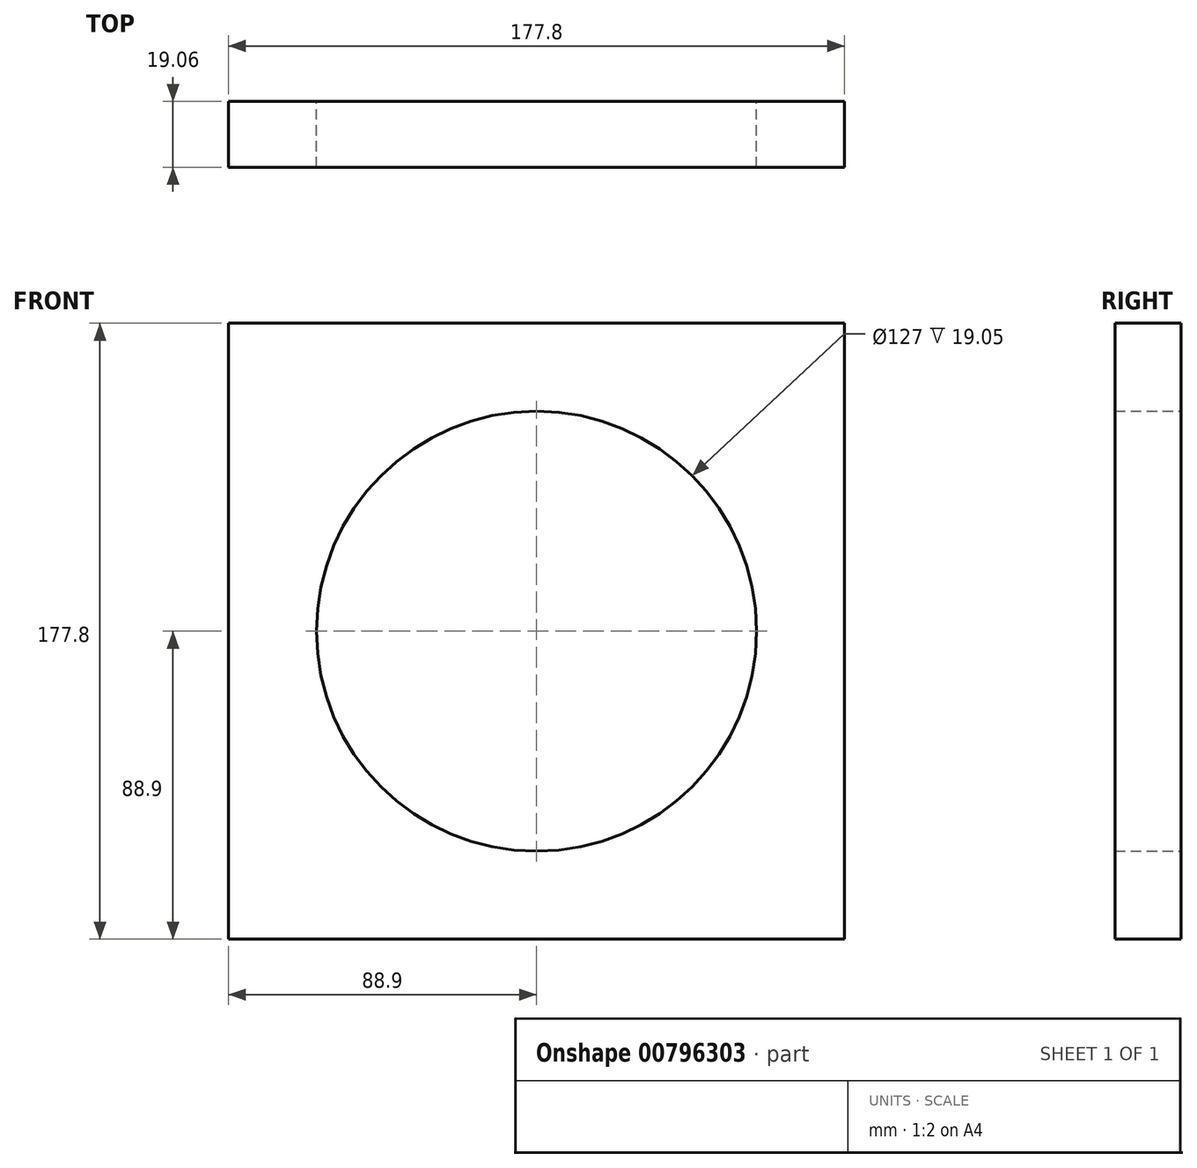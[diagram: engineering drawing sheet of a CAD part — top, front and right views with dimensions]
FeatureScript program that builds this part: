
annotation { "Feature Type Name" : "Feature", "Feature Type Description" : "" }
export const myFeature = defineFeature(function(context is Context, id is Id, definition is map)
    precondition{}
    {
        {
            var Q0;
            Q0=qCreatedBy(makeId("Front.planeOp"),FACE);
            var sketch = newSketch(context, id + "F0", { "sketchPlane" : qUnion([Q0])});
            skLineSegment(sketch, "E0.bottom", {"start": v(-88.9, 88.9) * mm, "end": v(88.9, 88.9) * mm});
            skLineSegment(sketch, "E0.top", {"start": v(-88.9, -88.9) * mm, "end": v(88.9, -88.9) * mm});
            skLineSegment(sketch, "E0.left", {"start": v(-88.9, 88.9) * mm, "end": v(-88.9, -88.9) * mm});
            skLineSegment(sketch, "E0.right", {"start": v(88.9, 88.9) * mm, "end": v(88.9, -88.9) * mm});
            skPoint(sketch, "E0.middle", {"position": v(0, 0) * mm});
            skSolve(sketch);
        }
        {
            var Q0;
            Q0=makeQuery(id+"F0.imprint","IMPRINT",FACE,{"disambiguationData":[TD([[makeQuery(id+"F0.imprint","IMPRINT",EDGE,{"derivedFrom":sQuery(id+"F0.wireOp",EDGE,"E0.bottom")}),-1.0]])]});
            var sketch = newSketch(context, id + "F1", { "sketchPlane" : qUnion([Q0])});
            skCircle(sketch, "E1", {"center": v(0, 0) * mm, "radius": 63.5 * mm});
            skSolve(sketch);
        }
        {
            var Q0;
            Q0=makeQuery(id+"F1.imprint","IMPRINT",FACE,{"disambiguationData":[TD([[makeQuery(id+"F1.imprint","IMPRINT",EDGE,{"derivedFrom":sQuery(id+"F1.wireOp",EDGE,"E1")}),-1.0]])]});
            extrude(context, id + "F2", {"entities" : qUnion([Q0]), "endBound" : BoundingType.SYMMETRIC, "depth" : 19.05 * mm, "offsetDistance" : 25.4 * mm});
        }
    });
